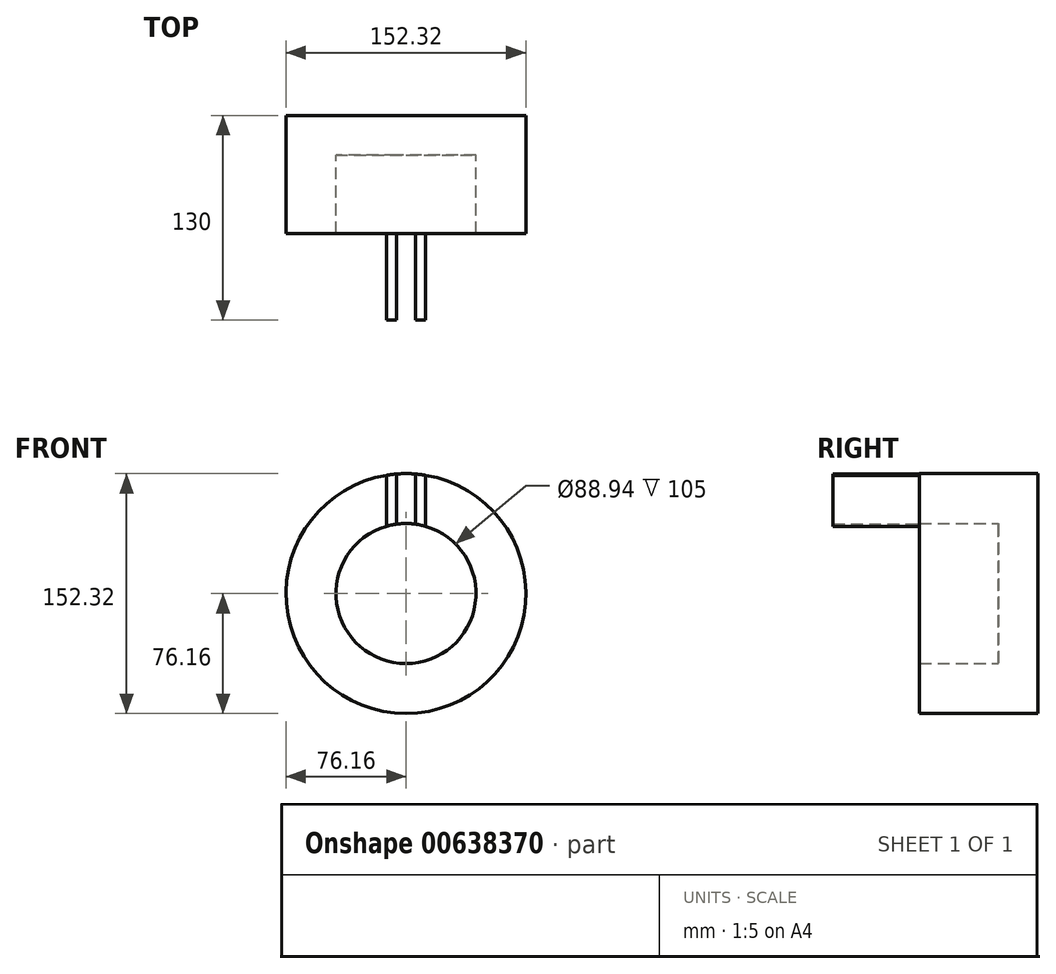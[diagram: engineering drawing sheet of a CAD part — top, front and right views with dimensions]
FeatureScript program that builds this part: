
annotation { "Feature Type Name" : "Feature", "Feature Type Description" : "" }
export const myFeature = defineFeature(function(context is Context, id is Id, definition is map)
    precondition{}
    {
        {
            var Q0;
            Q0=qCreatedBy(makeId("Front.planeOp"),FACE);
            var sketch = newSketch(context, id + "F0", { "sketchPlane" : qUnion([Q0])});
            skCircle(sketch, "E0", {"center": v(0, 0) * mm, "radius": 76.16 * mm});
            skSolve(sketch);
        }
        {
            var Q0;
            Q0=makeQuery(id+"F0.imprint","IMPRINT",FACE,{"disambiguationData":[TD([[makeQuery(id+"F0.imprint","IMPRINT",EDGE,{"derivedFrom":sQuery(id+"F0.wireOp",EDGE,"E0")}),1.0]])]});
            var sketch = newSketch(context, id + "F1", { "sketchPlane" : qUnion([Q0])});
            skSolve(sketch);
        }
        {
            var Q0;
            Q0=makeQuery(id+"F1.imprint","IMPRINT",FACE,{"disambiguationData":[TD([[makeQuery(id+"F1.imprint","IMPRINT",EDGE,{"derivedFrom":makeQuery(id+"F0.imprint","IMPRINT",EDGE,{"derivedFrom":sQuery(id+"F0.wireOp",EDGE,"E0")})}),1.0]])]});
            extrude(context, id + "F2", {"entities" : qUnion([Q0]), "depth" : 25 * mm, "offsetDistance" : 25 * mm});
        }
        {
            var Q0;
            Q0=makeQuery(id+"F2.opExtrude","CAP_FACE",FACE,{"disambiguationData":[OSD([sQuery(id+"F0.wireOp",EDGE,"E0")])],"isStart":false});
            var sketch = newSketch(context, id + "F3", { "sketchPlane" : qUnion([Q0])});
            skCircle(sketch, "E1", {"center": v(0, 0) * mm, "radius": 44.47 * mm});
            skSolve(sketch);
        }
        {
            var Q0;
            Q0=makeQuery(id+"F3.imprint","IMPRINT",FACE,{"disambiguationData":[TD([[makeQuery(id+"F3.imprint","IMPRINT",EDGE,{"derivedFrom":sQuery(id+"F3.wireOp",EDGE,"E1")}),-1.0]])]});
            var sketch = newSketch(context, id + "F4", { "sketchPlane" : qUnion([Q0])});
            skLineSegment(sketch, "E2", {"start": v(-12.81, 22.4) * mm, "end": v(-12.81, 74.76) * mm});
            skLineSegment(sketch, "E3", {"start": v(12.44, 22.03) * mm, "end": v(12.44, 75.5) * mm});
            skSolve(sketch);
        }
        {
            var Q0;
            Q0=makeQuery(id+"F4.imprint","IMPRINT",FACE,{"disambiguationData":[TD([[makeQuery(id+"F4.imprint","IMPRINT",EDGE,{"derivedFrom":makeQuery(id+"F3.imprint","IMPRINT",EDGE,{"derivedFrom":makeQuery(id+"F2.opExtrude","CAP_EDGE",EDGE,{"disambiguationData":[OSD([sQuery(id+"F0.wireOp",EDGE,"E0")])],"isStart":false})})}),1.0]])]});
            extrude(context, id + "F5", {"entities" : qUnion([Q0]), "operationType" : NewBodyOperationType.ADD, "depth" : 50 * mm, "offsetDistance" : 25 * mm});
        }
        {
            var Q0;
            Q0=makeQuery(id+"F5.opExtrude","CAP_FACE",FACE,{"disambiguationData":[OSD([sQuery(id+"F0.wireOp",EDGE,"E0"),sQuery(id+"F3.wireOp",EDGE,"E1")])],"isStart":false});
            var sketch = newSketch(context, id + "F6", { "sketchPlane" : qUnion([Q0])});
            skLineSegment(sketch, "E4", {"start": v(-12.44, 21.32) * mm, "end": v(-12.44, 75.14) * mm});
            skLineSegment(sketch, "E5", {"start": v(-12.44, 75.14) * mm, "end": v(-5.98, 75.92) * mm});
            skLineSegment(sketch, "E6", {"start": v(-5.98, 75.92) * mm, "end": v(-5.98, 44.06) * mm});
            skLineSegment(sketch, "E7", {"start": v(-5.98, 44.06) * mm, "end": v(-7.47, 38.66) * mm});
            skLineSegment(sketch, "E8", {"start": v(-7.47, 38.66) * mm, "end": v(-7.47, 21.5) * mm});
            skLineSegment(sketch, "E9", {"start": v(12.44, 21.88) * mm, "end": v(12.44, 75.14) * mm});
            skLineSegment(sketch, "E10", {"start": v(12.44, 75.14) * mm, "end": v(6.17, 75.9) * mm});
            skLineSegment(sketch, "E11", {"start": v(6.17, 75.9) * mm, "end": v(6.17, 44.04) * mm});
            skLineSegment(sketch, "E12", {"start": v(6.17, 44.04) * mm, "end": v(7.84, 39.2) * mm});
            skLineSegment(sketch, "E13", {"start": v(7.84, 39.2) * mm, "end": v(7.84, 21.7) * mm});
            skLineSegment(sketch, "E14", {"start": v(7.84, 21.7) * mm, "end": v(-7.47, 21.5) * mm});
            skLineSegment(sketch, "E15", {"start": v(-5.98, 75.92) * mm, "end": v(6.17, 75.9) * mm});
            skSolve(sketch);
        }
        {
            var Q0;
            {var subQ0=sQuery(id+"F6.wireOp",EDGE,"E10");Q0=makeQuery(id+"F6.imprint","IMPRINT",FACE,{"disambiguationData":[TD([[makeQuery(id+"F6.imprint","IMPRINT",EDGE,{"derivedFrom":subQ0}),1.0]])]});}
            var Q1;
            {var subQ0=sQuery(id+"F6.wireOp",EDGE,"E5");Q1=makeQuery(id+"F6.imprint","IMPRINT",FACE,{"disambiguationData":[TD([[makeQuery(id+"F6.imprint","IMPRINT",EDGE,{"derivedFrom":subQ0}),-1.0]])]});}
            extrude(context, id + "F7", {"entities" : qUnion([Q0, Q1]), "operationType" : NewBodyOperationType.ADD, "depth" : 55 * mm, "offsetDistance" : 25 * mm});
        }
    });
